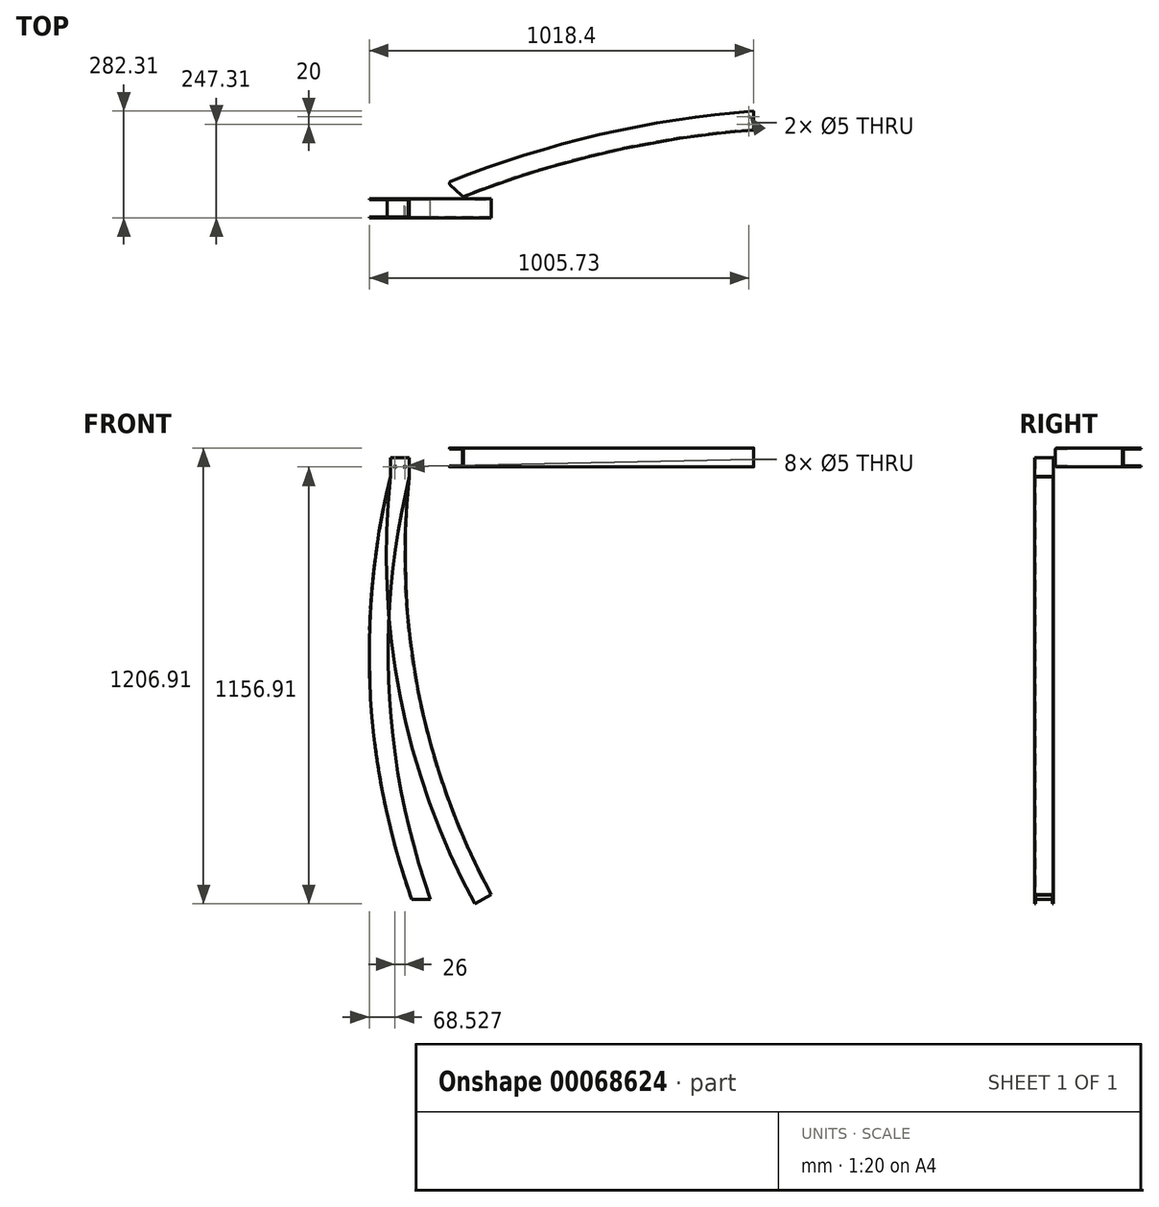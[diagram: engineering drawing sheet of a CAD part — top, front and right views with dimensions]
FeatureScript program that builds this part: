
annotation { "Feature Type Name" : "Feature", "Feature Type Description" : "" }
export const myFeature = defineFeature(function(context is Context, id is Id, definition is map)
    precondition{}
    {
        {
            var Q0;
            Q0=qCreatedBy(makeId("Right.planeOp"),FACE);
            var sketch = newSketch(context, id + "F0", { "sketchPlane" : qUnion([Q0])});
            skLineSegment(sketch, "E0.bottom", {"start": v(25, 25) * mm, "end": v(-25, 25) * mm});
            skLineSegment(sketch, "E0.top", {"start": v(25, -25) * mm, "end": v(-25, -25) * mm});
            skLineSegment(sketch, "E0.left", {"start": v(25, 25) * mm, "end": v(25, -25) * mm});
            skLineSegment(sketch, "E0.right", {"start": v(-25, 25) * mm, "end": v(-25, -25) * mm});
            skSolve(sketch);
        }
        {
            var Q0;
            Q0=qCreatedBy(makeId("Top.planeOp"),FACE);
            var sketch = newSketch(context, id + "F1", { "sketchPlane" : qUnion([Q0])});
            skLineSegment(sketch, "E1", {"start": v(0, 0) * mm, "end": v(-246.2, -43.41) * mm, "construction": true});
            skLineSegment(sketch, "E2", {"start": v(-246.2, -43.41) * mm, "end": v(-481.13, -128.92) * mm, "construction": true});
            skLineSegment(sketch, "E3", {"start": v(-481.13, -128.92) * mm, "end": v(-697.63, -253.92) * mm, "construction": true});
            skPoint(sketch, "E4", {"position": v(-802.75, -188.6) * mm});
            skArc(sketch, "E5", {"start": v(0, 0) * mm, "mid": v(-408.69, -63.18) * mm, "end": v(-802.75, -188.6) * mm});
            skSolve(sketch);
        }
        {
            var Q0;
            Q0 = qSketchRegion(id + "F0", true);
            var Q1;
            Q1=sQuery(id+"F1.wireOp",EDGE,"E5");
            sweep(context, id + "F2", {"profiles" : qUnion([Q0]), "path" : qUnion([Q1])});
        }
        {
            var Q0;
            Q0=qCreatedBy(makeId("Top.planeOp"),FACE);
            var sketch = newSketch(context, id + "F3", { "sketchPlane" : qUnion([Q0])});
            skLineSegment(sketch, "E6", {"start": v(-810.37, -164.79) * mm, "end": v(-795.14, -212.41) * mm});
            skLineSegment(sketch, "E7", {"start": v(-795.14, -212.41) * mm, "end": v(-767.65, -203.62) * mm});
            skLineSegment(sketch, "E8", {"start": v(-767.65, -203.62) * mm, "end": v(-810.37, -164.79) * mm});
            skSolve(sketch);
        }
        {
            var Q0;
            Q0 = qSketchRegion(id + "F3", true);
            extrude(context, id + "F4", {"entities" : qUnion([Q0]), "operationType" : NewBodyOperationType.REMOVE, "endBound" : BoundingType.SYMMETRIC, "oppositeDirection" : true, "depth" : 60 * mm});
        }
        {
            var Q0;
            Q0=makeQuery(id+"F2.opSweep","SWEPT_FACE",FACE,{"disambiguationData":[OSD([sQuery(id+"F0.wireOp",EDGE,"E0.left"),sQuery(id+"F1.wireOp",EDGE,"E5")])]});
            var Q1;
            Q1=makeQuery(id+"F4.boolean.opBoolean","COPY",FACE,{"derivedFrom":makeQuery(id+"F4.opExtrude","SWEPT_FACE",FACE,{"disambiguationData":[OSD([sQuery(id+"F3.wireOp",EDGE,"E8")])]})});
            var Q2;
            Q2=makeQuery(id+"F2.opSweep","CAP_FACE",FACE,{"disambiguationData":[OSD([sQuery(id+"F0.wireOp",EDGE,"E0.bottom"),sQuery(id+"F0.wireOp",EDGE,"E0.top"),sQuery(id+"F0.wireOp",EDGE,"E0.left"),sQuery(id+"F0.wireOp",EDGE,"E0.right"),sQuery(id+"F1.wireOp",VERTEX,"E5.start")])],"isStart":true});
            var Q3;
            Q3=makeQuery(id+"F2.opSweep","SWEPT_BODY",BODY,{"disambiguationData":[OSD([sQuery(id+"F0.wireOp",EDGE,"E0.bottom"),sQuery(id+"F0.wireOp",EDGE,"E0.top"),sQuery(id+"F0.wireOp",EDGE,"E0.left"),sQuery(id+"F0.wireOp",EDGE,"E0.right"),sQuery(id+"F1.wireOp",EDGE,"E5")])]});
            shell(context, id + "F5", {"entities" : qUnion([Q0, Q1, Q2]), "parts" : qUnion([Q3]), "thickness" : 2.5 * mm});
        }
        {
            var Q0;
            Q0=qCreatedBy(makeId("Top.planeOp"),FACE);
            var sketch = newSketch(context, id + "F6", { "sketchPlane" : qUnion([Q0])});
            skCircle(sketch, "E9", {"center": v(-12.67, 10) * mm, "radius": 2.5 * mm});
            skCircle(sketch, "E10", {"center": v(-12.67, -10) * mm, "radius": 2.5 * mm});
            skSolve(sketch);
        }
        {
            var Q0;
            Q0 = qSketchRegion(id + "F6", true);
            extrude(context, id + "F7", {"entities" : qUnion([Q0]), "operationType" : NewBodyOperationType.REMOVE, "oppositeDirection" : true, "depth" : 25 * mm});
        }
        {
            var Q0;
            Q0=makeQuery(id+"F2.opSweep","SWEPT_EDGE",EDGE,{"disambiguationData":[OSD([sQuery(id+"F0.wireOp",EDGE,"E0.top"),sQuery(id+"F0.wireOp",EDGE,"E0.right"),sQuery(id+"F1.wireOp",EDGE,"vZhR8UCJ-6n1K-2ejP-Ha9e-Ch7yrhJ1cl9g")])]});
            var Q1;
            Q1=makeQuery(id+"F2.opSweep","SWEPT_EDGE",EDGE,{"disambiguationData":[OSD([sQuery(id+"F0.wireOp",EDGE,"E0.bottom"),sQuery(id+"F0.wireOp",EDGE,"E0.right"),sQuery(id+"F1.wireOp",EDGE,"vZhR8UCJ-6n1K-2ejP-Ha9e-Ch7yrhJ1cl9g")])]});
            var Q2;
            Q2=makeQuery(id+"F4.boolean.opBoolean","MERGE",EDGE,{"derivedFrom":[makeQuery(id+"F2.opSweep","CAP_EDGE",EDGE,{"disambiguationData":[OSD([sQuery(id+"F0.wireOp",EDGE,"E0.left"),sQuery(id+"F1.wireOp",VERTEX,"E5.end")])],"isStart":false}),makeQuery(id+"F4.opExtrude","SWEPT_EDGE",EDGE,{"disambiguationData":[OSD([sQuery(id+"F3.wireOp",EDGE,"E6"),sQuery(id+"F3.wireOp",EDGE,"E8")])]})]});
            var Q3;
            Q3=makeQuery(id+"F5.opShell","OFFSET_EDGE",EDGE,{"disambiguationData":[OSD([sQuery(id+"F0.wireOp",EDGE,"E0.left"),sQuery(id+"F1.wireOp",VERTEX,"E5.end"),sQuery(id+"F3.wireOp",EDGE,"E6"),sQuery(id+"F3.wireOp",EDGE,"E8")])]});
            fillet(context, id + "F8", {"entities" : qUnion([Q0, Q1, Q2, Q3]), "radius" : 5 * mm, "tangentPropagation" : true, "allowEdgeOverflow" : false});
        }
        {
            var Q0;
            Q0=qCreatedBy(makeId("Top.planeOp"),FACE);
            var sketch = newSketch(context, id + "F9", { "sketchPlane" : qUnion([Q0])});
            skLineSegment(sketch, "E11.bottom", {"start": v(-911.87, -257.31) * mm, "end": v(-961.87, -257.31) * mm});
            skLineSegment(sketch, "E11.top", {"start": v(-911.87, -207.31) * mm, "end": v(-961.87, -207.31) * mm});
            skLineSegment(sketch, "E11.left", {"start": v(-911.87, -257.31) * mm, "end": v(-911.87, -207.31) * mm});
            skLineSegment(sketch, "E11.right", {"start": v(-961.87, -257.31) * mm, "end": v(-961.87, -207.31) * mm});
            skPoint(sketch, "E11.middle", {"position": v(-936.87, -232.31) * mm});
            skSolve(sketch);
        }
        {
            var Q0;
            Q0=sQuery(id+"F9.wireOp",EDGE,"E11.top");
            cPoint(context, id + "F10", {"entities" : qUnion([Q0]), "parameter" : 0.5});
        }
        {
            var Q0;
            Q0=sQuery(id+"F9.wireOp",EDGE,"E11.bottom");
            cPoint(context, id + "F11", {"entities" : qUnion([Q0]), "parameter" : 0.5});
        }
        {
            var Q0;
            Q0 = qCreatedBy(id + "F10" ,VERTEX);
            var Q1;
            Q1 = qCreatedBy(id + "F11" ,VERTEX);
            cPlane(context, id + "F12", {"entities" : qUnion([Q0, Q1]), "cplaneType" : CPlaneType.MID_PLANE, "offset" : 25 * mm, "width" : 150 * mm, "height" : 150 * mm});
        }
        {
            var Q0;
            Q0=qCreatedBy(id+"F12.planeOp",FACE);
            var sketch = newSketch(context, id + "F13", { "sketchPlane" : qUnion([Q0])});
            skPoint(sketch, "E12", {"position": v(-936.87, 0) * mm});
            skPoint(sketch, "E13", {"position": v(-716.68, -1170) * mm});
            skPoint(sketch, "E14", {"position": v(-936.87, -50) * mm});
            skLineSegment(sketch, "E15", {"start": v(-936.87, 0) * mm, "end": v(-936.87, -50) * mm});
            skArc(sketch, "E16", {"start": v(-936.87, -50) * mm, "mid": v(-912.16, -626.79) * mm, "end": v(-716.68, -1170) * mm});
            skLineSegment(sketch, "E17", {"start": v(-1176.13, 0) * mm, "end": v(-1176.13, -50) * mm});
            skPoint(sketch, "E18", {"position": v(-1120.1, -1170) * mm});
            skArc(sketch, "E19", {"start": v(-1176.13, -50) * mm, "mid": v(-1230.22, -614.1) * mm, "end": v(-1120.1, -1170) * mm});
            skSolve(sketch);
        }
        {
            var Q0;
            Q0 = qSketchRegion(id + "F9", true);
            var Q1;
            Q1=sQuery(id+"F13.wireOp",EDGE,"E15");
            var Q2;
            Q2=sQuery(id+"F13.wireOp",EDGE,"E16");
            sweep(context, id + "F14", {"profiles" : qUnion([Q0]), "path" : qUnion([Q1, Q2])});
        }
        {
            var Q0;
            Q0=makeQuery(id+"F14.opSweep","SWEPT_FACE",FACE,{"disambiguationData":[OSD([sQuery(id+"F9.wireOp",EDGE,"E11.right"),sQuery(id+"F13.wireOp",EDGE,"EIfQFfMN-x83m-lLxE-Jrmg-Q6QmkGi6PZSz")])]});
            var Q1;
            Q1=makeQuery(id+"F14.opSweep","CAP_FACE",FACE,{"disambiguationData":[OSD([sQuery(id+"F9.wireOp",EDGE,"E11.bottom"),sQuery(id+"F9.wireOp",EDGE,"E11.top"),sQuery(id+"F9.wireOp",EDGE,"E11.left"),sQuery(id+"F9.wireOp",EDGE,"E11.right"),sQuery(id+"F13.wireOp",VERTEX,"EIfQFfMN-x83m-lLxE-Jrmg-Q6QmkGi6PZSz.start")])],"isStart":true});
            var Q2;
            Q2=makeQuery(id+"F14.opSweep","CAP_FACE",FACE,{"disambiguationData":[OSD([sQuery(id+"F9.wireOp",EDGE,"E11.bottom"),sQuery(id+"F9.wireOp",EDGE,"E11.top"),sQuery(id+"F9.wireOp",EDGE,"E11.left"),sQuery(id+"F9.wireOp",EDGE,"E11.right"),sQuery(id+"F13.wireOp",VERTEX,"EIfQFfMN-x83m-lLxE-Jrmg-Q6QmkGi6PZSz.end")])],"isStart":false});
            shell(context, id + "F15", {"entities" : qUnion([Q0, Q1, Q2]), "thickness" : 2.5 * mm});
        }
        {
            var Q0;
            Q0 = qSketchRegion(id + "F9", true);
            var Q1;
            Q1=sQuery(id+"F13.wireOp",EDGE,"E17");
            var Q2;
            Q2=sQuery(id+"F13.wireOp",EDGE,"E19");
            sweep(context, id + "F16", {"profiles" : qUnion([Q0]), "path" : qUnion([Q1, Q2]), "keepProfileOrientation" : true});
        }
        {
            var Q0;
            Q0=makeQuery(id+"F16.opSweep","SWEPT_FACE",FACE,{"disambiguationData":[OSD([sQuery(id+"F9.wireOp",EDGE,"E11.right"),sQuery(id+"F13.wireOp",EDGE,"E19")])]});
            var Q1;
            Q1=makeQuery(id+"F16.opSweep","SWEPT_FACE",FACE,{"disambiguationData":[OSD([sQuery(id+"F9.wireOp",EDGE,"E11.right"),sQuery(id+"F13.wireOp",EDGE,"E17")])]});
            var Q2;
            Q2=makeQuery(id+"F16.opSweep","CAP_FACE",FACE,{"disambiguationData":[OSD([sQuery(id+"F9.wireOp",EDGE,"E11.bottom"),sQuery(id+"F9.wireOp",EDGE,"E11.top"),sQuery(id+"F9.wireOp",EDGE,"E11.left"),sQuery(id+"F9.wireOp",EDGE,"E11.right"),sQuery(id+"F13.wireOp",VERTEX,"E17.start")])],"isStart":true});
            var Q3;
            Q3=makeQuery(id+"F16.opSweep","CAP_FACE",FACE,{"disambiguationData":[OSD([sQuery(id+"F9.wireOp",EDGE,"E11.bottom"),sQuery(id+"F9.wireOp",EDGE,"E11.top"),sQuery(id+"F9.wireOp",EDGE,"E11.left"),sQuery(id+"F9.wireOp",EDGE,"E11.right"),sQuery(id+"F13.wireOp",VERTEX,"E19.end")])],"isStart":false});
            shell(context, id + "F17", {"entities" : qUnion([Q0, Q1, Q2, Q3]), "thickness" : 2 * mm});
        }
        {
            var Q0;
            Q0=qCreatedBy(id+"F12.planeOp",FACE);
            var sketch = newSketch(context, id + "F18", { "sketchPlane" : qUnion([Q0])});
            skCircle(sketch, "E20", {"center": v(-923.87, -25) * mm, "radius": 2.5 * mm});
            skCircle(sketch, "E21", {"center": v(-949.87, -25) * mm, "radius": 2.5 * mm});
            skSolve(sketch);
        }
        {
            var Q0;
            Q0 = qSketchRegion(id + "F18", true);
            extrude(context, id + "F19", {"entities" : qUnion([Q0]), "operationType" : NewBodyOperationType.REMOVE, "endBound" : BoundingType.SYMMETRIC, "oppositeDirection" : true, "depth" : 60 * mm});
        }
    });
